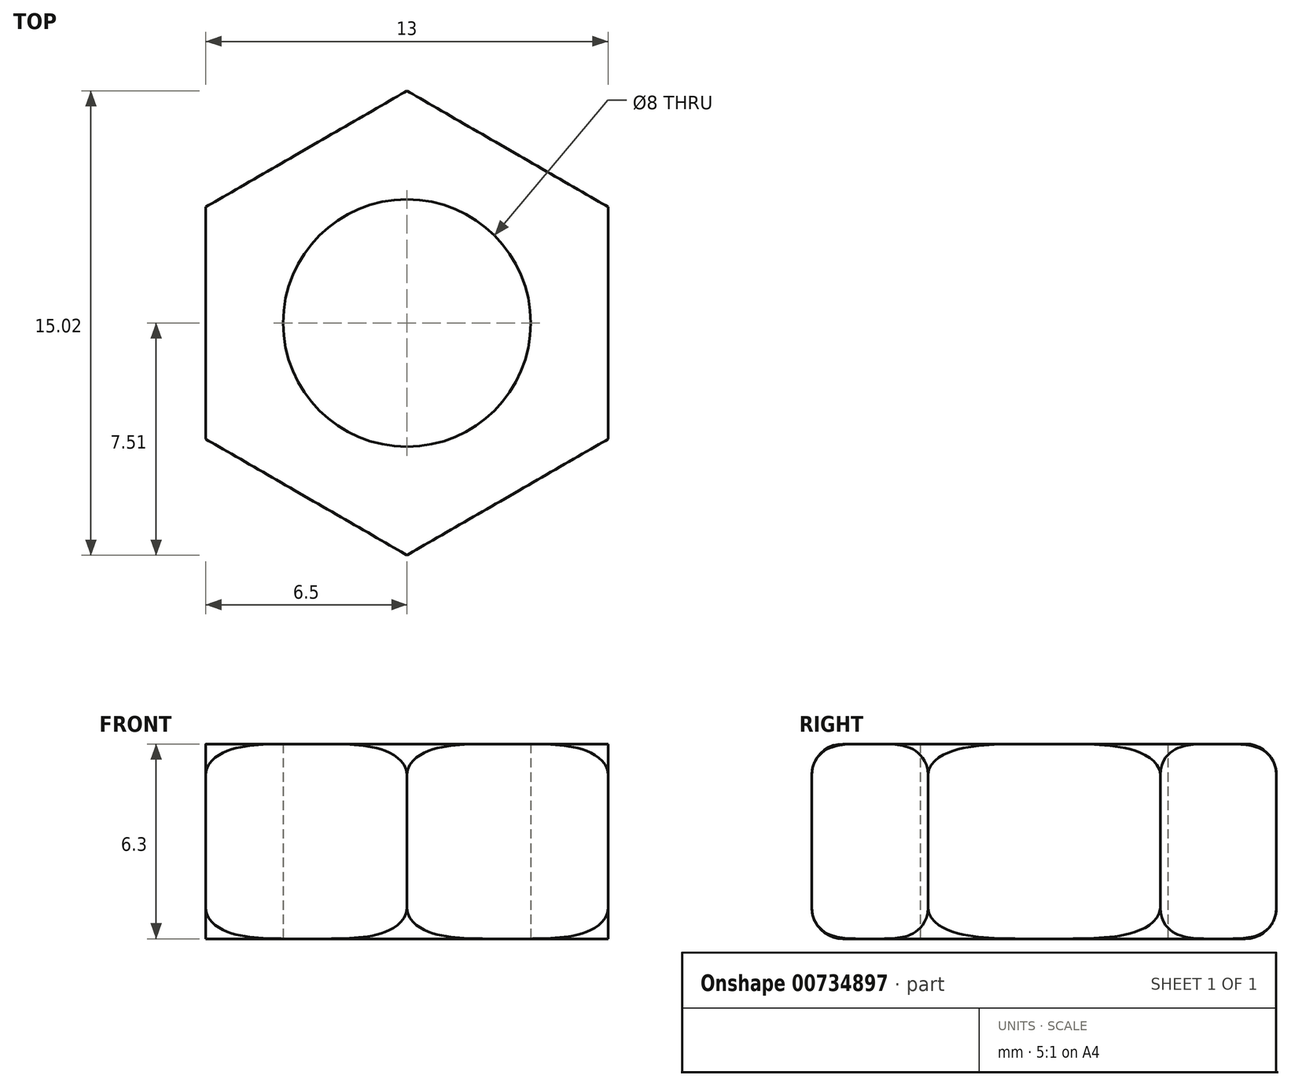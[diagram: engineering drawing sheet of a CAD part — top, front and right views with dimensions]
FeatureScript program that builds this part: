
annotation { "Feature Type Name" : "Feature", "Feature Type Description" : "" }
export const myFeature = defineFeature(function(context is Context, id is Id, definition is map)
    precondition{}
    {
        {
            var Q0;
            Q0=qCreatedBy(makeId("Top.planeOp"),FACE);
            var sketch = newSketch(context, id + "F0", { "sketchPlane" : qUnion([Q0])});
            skCircle(sketch, "E0.cCircle", {"center": v(0, 0) * mm, "radius": 6.5 * mm, "construction": true});
            skLineSegment(sketch, "E0.0", {"start": v(-6.5, -3.75) * mm, "end": v(-6.5, 3.75) * mm});
            skLineSegment(sketch, "E0.1", {"start": v(-6.5, 3.75) * mm, "end": v(0, 7.5) * mm});
            skLineSegment(sketch, "E0.2", {"start": v(0, 7.5) * mm, "end": v(6.5, 3.75) * mm});
            skLineSegment(sketch, "E0.3", {"start": v(6.5, 3.75) * mm, "end": v(6.5, -3.75) * mm});
            skLineSegment(sketch, "E0.4", {"start": v(6.5, -3.75) * mm, "end": v(0, -7.5) * mm});
            skLineSegment(sketch, "E0.5", {"start": v(0, -7.5) * mm, "end": v(-6.5, -3.75) * mm});
            skCircle(sketch, "E1", {"center": v(0, 0) * mm, "radius": 7.5 * mm});
            skCircle(sketch, "E2", {"center": v(0, 0) * mm, "radius": 4 * mm});
            skSolve(sketch);
        }
        {
            var Q0;
            {var subQ0=sQuery(id+"F0.wireOp",EDGE,"E0.0");Q0=makeQuery(id+"F0.imprint","IMPRINT",FACE,{"disambiguationData":[TD([[makeQuery(id+"F0.imprint","IMPRINT",EDGE,{"derivedFrom":subQ0}),1.0]])]});}
            var Q1;
            {var subQ0=sQuery(id+"F0.wireOp",EDGE,"E0.1");Q1=makeQuery(id+"F0.imprint","IMPRINT",FACE,{"disambiguationData":[TD([[makeQuery(id+"F0.imprint","IMPRINT",EDGE,{"derivedFrom":subQ0}),1.0]])]});}
            var Q2;
            {var subQ0=sQuery(id+"F0.wireOp",EDGE,"E0.2");Q2=makeQuery(id+"F0.imprint","IMPRINT",FACE,{"disambiguationData":[TD([[makeQuery(id+"F0.imprint","IMPRINT",EDGE,{"derivedFrom":subQ0}),1.0]])]});}
            var Q3;
            Q3=makeQuery(id+"F0.imprint","IMPRINT",FACE,{"disambiguationData":[TD([[makeQuery(id+"F0.imprint","IMPRINT",EDGE,{"derivedFrom":sQuery(id+"F0.wireOp",EDGE,"E0.0")}),-1.0]])]});
            var Q4;
            {var subQ0=sQuery(id+"F0.wireOp",EDGE,"E0.5");Q4=makeQuery(id+"F0.imprint","IMPRINT",FACE,{"disambiguationData":[TD([[makeQuery(id+"F0.imprint","IMPRINT",EDGE,{"derivedFrom":subQ0}),1.0]])]});}
            var Q5;
            {var subQ0=sQuery(id+"F0.wireOp",EDGE,"E0.3");Q5=makeQuery(id+"F0.imprint","IMPRINT",FACE,{"disambiguationData":[TD([[makeQuery(id+"F0.imprint","IMPRINT",EDGE,{"derivedFrom":subQ0}),1.0]])]});}
            var Q6;
            {var subQ0=sQuery(id+"F0.wireOp",EDGE,"E0.4");Q6=makeQuery(id+"F0.imprint","IMPRINT",FACE,{"disambiguationData":[TD([[makeQuery(id+"F0.imprint","IMPRINT",EDGE,{"derivedFrom":subQ0}),1.0]])]});}
            extrude(context, id + "F1", {"entities" : qUnion([Q0, Q1, Q2, Q3, Q4, Q5, Q6]), "endBound" : BoundingType.SYMMETRIC, "depth" : 6.3 * mm, "offsetDistance" : 25 * mm});
        }
        {
            var Q0;
            Q0=makeQuery(id+"F1.opExtrude","CAP_EDGE",EDGE,{"disambiguationData":[OSD([sQuery(id+"F0.wireOp",EDGE,"E1")])],"isStart":true});
            var Q1;
            Q1=makeQuery(id+"F1.opExtrude","CAP_EDGE",EDGE,{"disambiguationData":[OSD([sQuery(id+"F0.wireOp",EDGE,"E1")])],"isStart":false});
            fillet(context, id + "F2", {"entities" : qUnion([Q0, Q1]), "radius" : 1 * mm, "tangentPropagation" : true, "allowEdgeOverflow" : false});
        }
        {
            var Q0;
            {var subQ0=sQuery(id+"F0.wireOp",EDGE,"E0.0");Q0=makeQuery(id+"F0.imprint","IMPRINT",FACE,{"disambiguationData":[TD([[makeQuery(id+"F0.imprint","IMPRINT",EDGE,{"derivedFrom":subQ0}),1.0]])]});}
            var Q1;
            {var subQ0=sQuery(id+"F0.wireOp",EDGE,"E0.1");Q1=makeQuery(id+"F0.imprint","IMPRINT",FACE,{"disambiguationData":[TD([[makeQuery(id+"F0.imprint","IMPRINT",EDGE,{"derivedFrom":subQ0}),1.0]])]});}
            var Q2;
            {var subQ0=sQuery(id+"F0.wireOp",EDGE,"E0.2");Q2=makeQuery(id+"F0.imprint","IMPRINT",FACE,{"disambiguationData":[TD([[makeQuery(id+"F0.imprint","IMPRINT",EDGE,{"derivedFrom":subQ0}),1.0]])]});}
            var Q3;
            {var subQ0=sQuery(id+"F0.wireOp",EDGE,"E0.3");Q3=makeQuery(id+"F0.imprint","IMPRINT",FACE,{"disambiguationData":[TD([[makeQuery(id+"F0.imprint","IMPRINT",EDGE,{"derivedFrom":subQ0}),1.0]])]});}
            var Q4;
            {var subQ0=sQuery(id+"F0.wireOp",EDGE,"E0.4");Q4=makeQuery(id+"F0.imprint","IMPRINT",FACE,{"disambiguationData":[TD([[makeQuery(id+"F0.imprint","IMPRINT",EDGE,{"derivedFrom":subQ0}),1.0]])]});}
            var Q5;
            {var subQ0=sQuery(id+"F0.wireOp",EDGE,"E0.5");Q5=makeQuery(id+"F0.imprint","IMPRINT",FACE,{"disambiguationData":[TD([[makeQuery(id+"F0.imprint","IMPRINT",EDGE,{"derivedFrom":subQ0}),1.0]])]});}
            extrude(context, id + "F3", {"entities" : qUnion([Q0, Q1, Q2, Q3, Q4, Q5]), "operationType" : NewBodyOperationType.REMOVE, "endBound" : BoundingType.SYMMETRIC, "depth" : 7 * mm, "offsetDistance" : 25 * mm});
        }
    });
